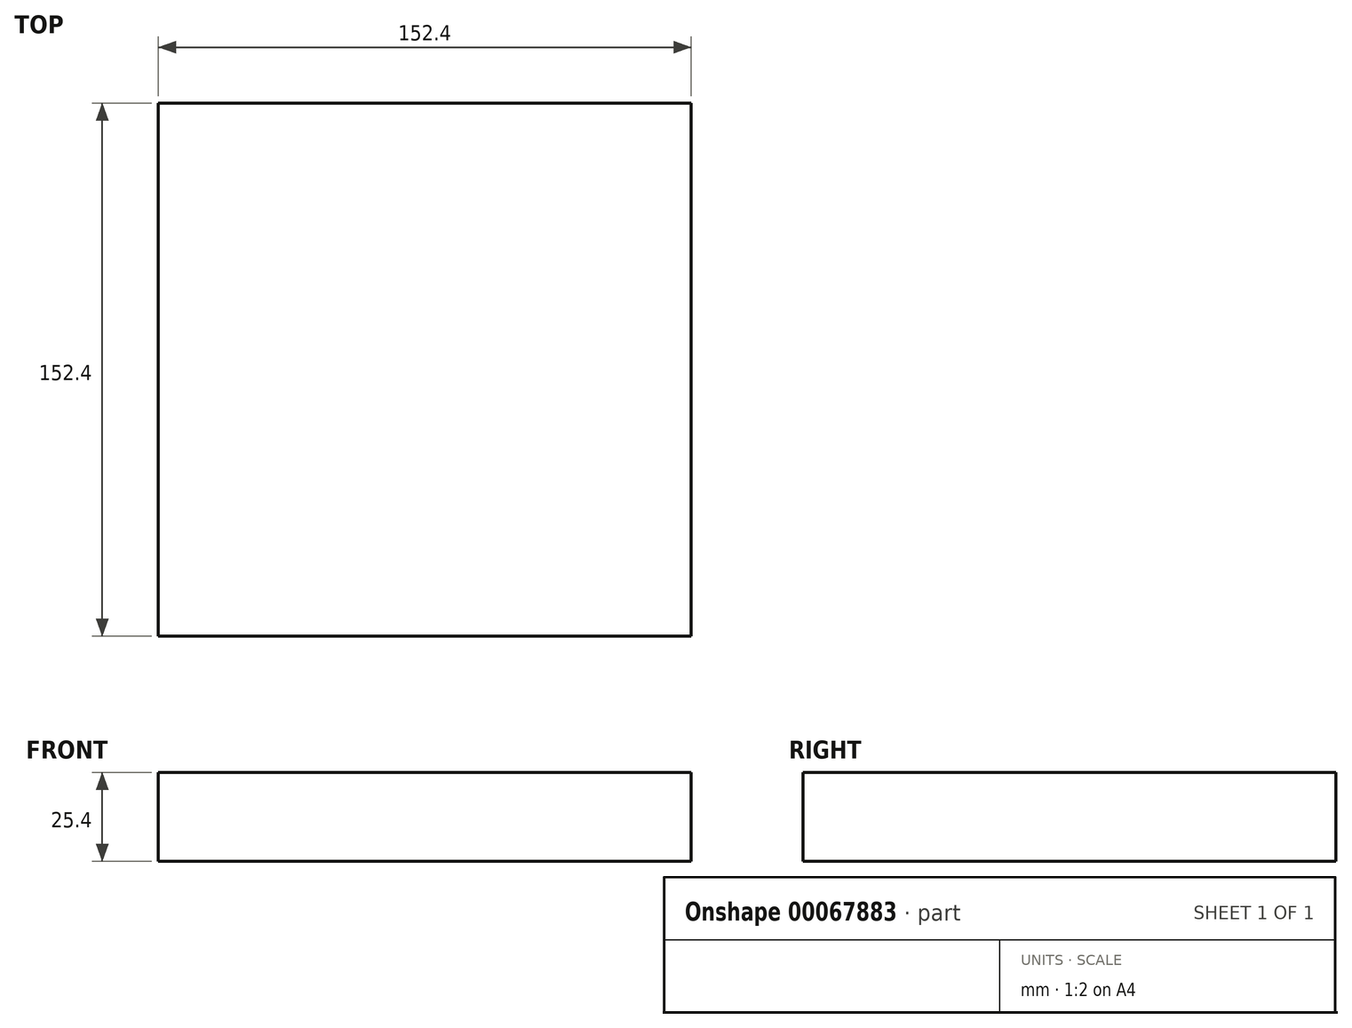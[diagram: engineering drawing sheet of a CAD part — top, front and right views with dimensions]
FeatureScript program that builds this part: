
annotation { "Feature Type Name" : "Feature", "Feature Type Description" : "" }
export const myFeature = defineFeature(function(context is Context, id is Id, definition is map)
    precondition{}
    {
        {
            var Q0;
            Q0=qCreatedBy(makeId("Top.planeOp"),FACE);
            var sketch = newSketch(context, id + "F0", { "sketchPlane" : qUnion([Q0])});
            skLineSegment(sketch, "E0.right", {"start": v(16.46, -47.28) * mm, "end": v(16.46, -47.28) * mm});
            skLineSegment(sketch, "E1.bottom", {"start": v(16.46, -47.28) * mm, "end": v(168.86, -47.28) * mm});
            skLineSegment(sketch, "E1.top", {"start": v(16.46, 105.12) * mm, "end": v(168.86, 105.12) * mm});
            skLineSegment(sketch, "E1.left", {"start": v(16.46, -47.28) * mm, "end": v(16.46, 105.12) * mm});
            skLineSegment(sketch, "E1.right", {"start": v(168.86, -47.28) * mm, "end": v(168.86, 105.12) * mm});
            skSolve(sketch);
        }
        {
            var Q0;
            Q0 = qSketchRegion(id + "F0", true);
            extrude(context, id + "F1", {"entities" : qUnion([Q0]), "depth" : 25.4 * mm});
        }
    });
